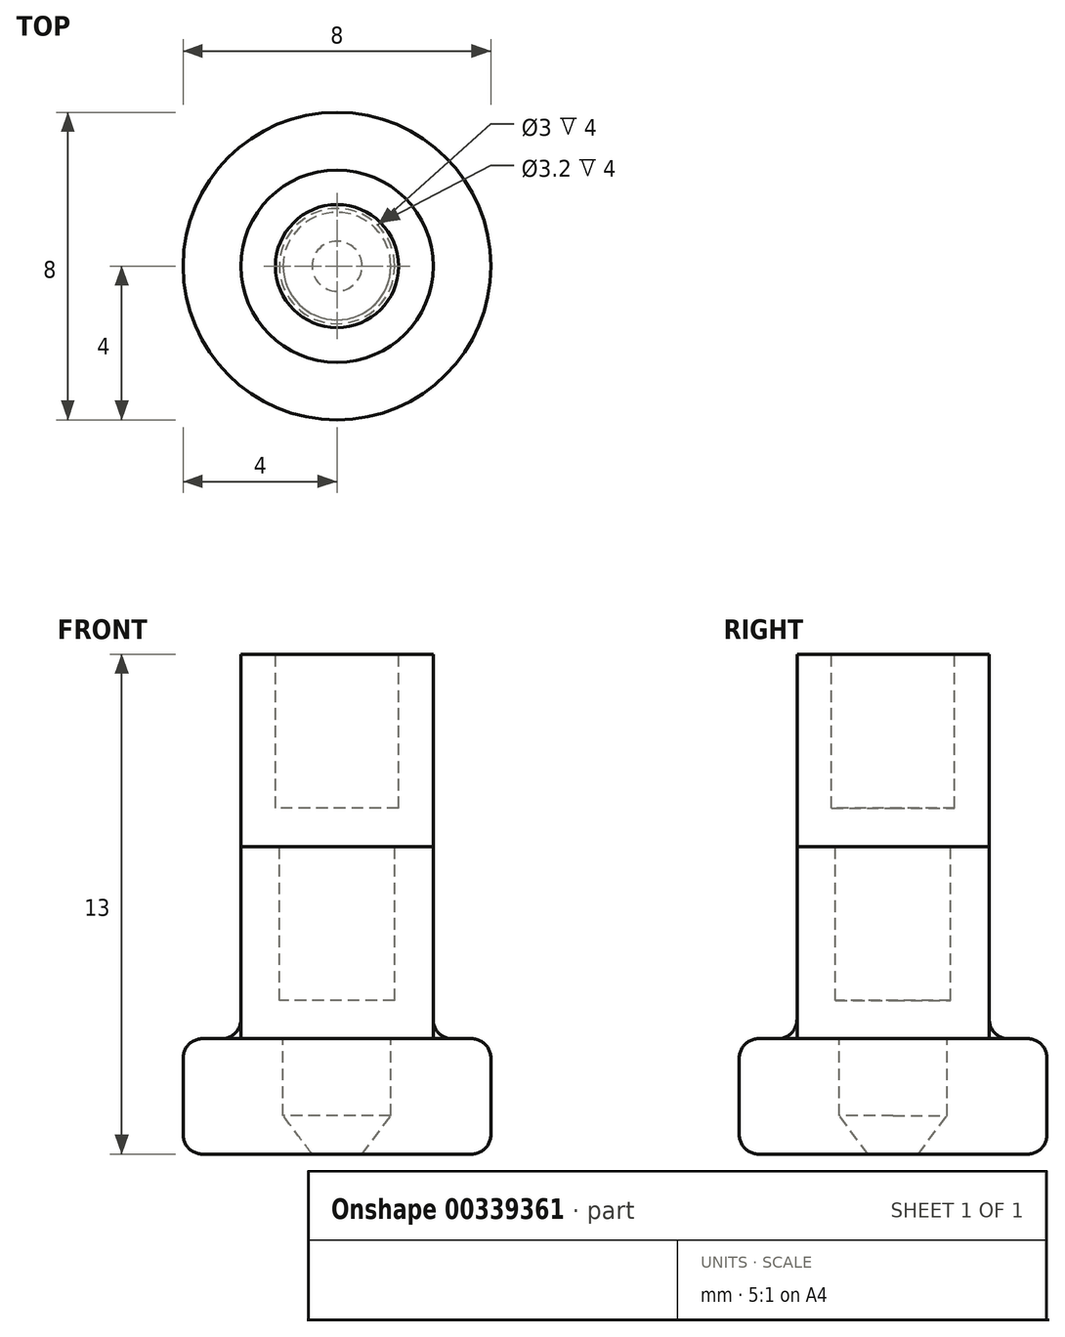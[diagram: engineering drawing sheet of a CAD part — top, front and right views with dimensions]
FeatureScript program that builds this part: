
annotation { "Feature Type Name" : "Feature", "Feature Type Description" : "" }
export const myFeature = defineFeature(function(context is Context, id is Id, definition is map)
    precondition{}
    {
        {
            var Q0;
            Q0=qCreatedBy(makeId("Front.planeOp"),FACE);
            var sketch = newSketch(context, id + "F0", { "sketchPlane" : qUnion([Q0])});
            skLineSegment(sketch, "E0", {"start": v(-1.6, 10) * mm, "end": v(-2.5, 10) * mm});
            skLineSegment(sketch, "E1", {"start": v(-2.5, 10) * mm, "end": v(-2.5, 0) * mm});
            skLineSegment(sketch, "E2", {"start": v(-2.5, 0) * mm, "end": v(-1.4, 0) * mm});
            skLineSegment(sketch, "E3", {"start": v(-1.4, 0) * mm, "end": v(-1.4, -3) * mm});
            skLineSegment(sketch, "E4", {"start": v(-1.4, -3) * mm, "end": v(0, -3) * mm});
            skLineSegment(sketch, "E5", {"start": v(-1.6, 10) * mm, "end": v(-1.6, 6) * mm});
            skLineSegment(sketch, "E6", {"start": v(-1.6, 6) * mm, "end": v(0, 6) * mm});
            skLineSegment(sketch, "E7", {"start": v(0, 6) * mm, "end": v(0, -3) * mm});
            skLineSegment(sketch, "E8", {"start": v(0, 7.91) * mm, "end": v(0, -7.96) * mm, "construction": true});
            skSolve(sketch);
        }
        {
            var Q0;
            Q0=makeQuery(id+"F0.imprint","IMPRINT",FACE,{"disambiguationData":[TD([[makeQuery(id+"F0.imprint","IMPRINT",EDGE,{"derivedFrom":sQuery(id+"F0.wireOp",EDGE,"E0")}),1.0]])]});
            var Q1;
            Q1=sQuery(id+"F0.wireOp",EDGE,"E8");
            revolve(context, id + "F1", {"entities" : qUnion([Q0]), "axis" : qUnion([Q1]), "revolveType" : RevolveType.FULL});
        }
        {
            var Q0;
            Q0=makeQuery(id+"F1.opRevolve","SWEPT_EDGE",EDGE,{"disambiguationData":[OSD([sQuery(id+"F0.wireOp",EDGE,"E3"),sQuery(id+"F0.wireOp",EDGE,"E4")])]});
            chamfer(context, id + "F2", {"entities" : qUnion([Q0]), "chamferType" : ChamferType.TWO_OFFSETS, "width1" : 1 * mm, "oppositeDirection" : false, "width2" : .75 * mm, "tangentPropagation" : true});
        }
        {
            var Q0;
            Q0=qCreatedBy(makeId("Front.planeOp"),FACE);
            var sketch = newSketch(context, id + "F3", { "sketchPlane" : qUnion([Q0])});
            skLineSegment(sketch, "E9", {"start": v(-1.5, 5) * mm, "end": v(-2.5, 5) * mm});
            skLineSegment(sketch, "E10", {"start": v(-2.5, 5) * mm, "end": v(-2.5, 0) * mm});
            skLineSegment(sketch, "E11", {"start": v(-4, 0) * mm, "end": v(-2.5, 0) * mm});
            skLineSegment(sketch, "E12", {"start": v(-1.5, 5) * mm, "end": v(-1.5, 1) * mm});
            skLineSegment(sketch, "E13", {"start": v(-1.5, 1) * mm, "end": v(0, 1) * mm});
            skLineSegment(sketch, "E14", {"start": v(0, 1) * mm, "end": v(0, -3) * mm});
            skLineSegment(sketch, "E15", {"start": v(0, 7.7) * mm, "end": v(0, -4.75) * mm, "construction": true});
            skLineSegment(sketch, "E16", {"start": v(-4, 0) * mm, "end": v(-4, -3) * mm});
            skLineSegment(sketch, "E17", {"start": v(-4, -3) * mm, "end": v(0, -3) * mm});
            skSolve(sketch);
        }
        {
            var Q0;
            Q0 = qSketchRegion(id + "F3", true);
            var Q1;
            Q1=sQuery(id+"F3.wireOp",EDGE,"E15");
            revolve(context, id + "F4", {"entities" : qUnion([Q0]), "axis" : qUnion([Q1]), "revolveType" : RevolveType.FULL});
        }
        {
            var Q0;
            Q0=makeQuery(id+"F4.opRevolve","SWEPT_EDGE",EDGE,{"disambiguationData":[OSD([sQuery(id+"F3.wireOp",EDGE,"E16"),sQuery(id+"F3.wireOp",EDGE,"E17")])]});
            var Q1;
            Q1=makeQuery(id+"F4.opRevolve","SWEPT_EDGE",EDGE,{"disambiguationData":[OSD([sQuery(id+"F3.wireOp",EDGE,"E11"),sQuery(id+"F3.wireOp",EDGE,"E16")])]});
            var Q2;
            Q2=makeQuery(id+"F4.opRevolve","SWEPT_EDGE",EDGE,{"disambiguationData":[OSD([sQuery(id+"F3.wireOp",EDGE,"E10"),sQuery(id+"F3.wireOp",EDGE,"E11")])]});
            fillet(context, id + "F5", {"entities" : qUnion([Q0, Q1, Q2]), "radius" : .5 * mm, "tangentPropagation" : true, "allowEdgeOverflow" : false});
        }
    });
